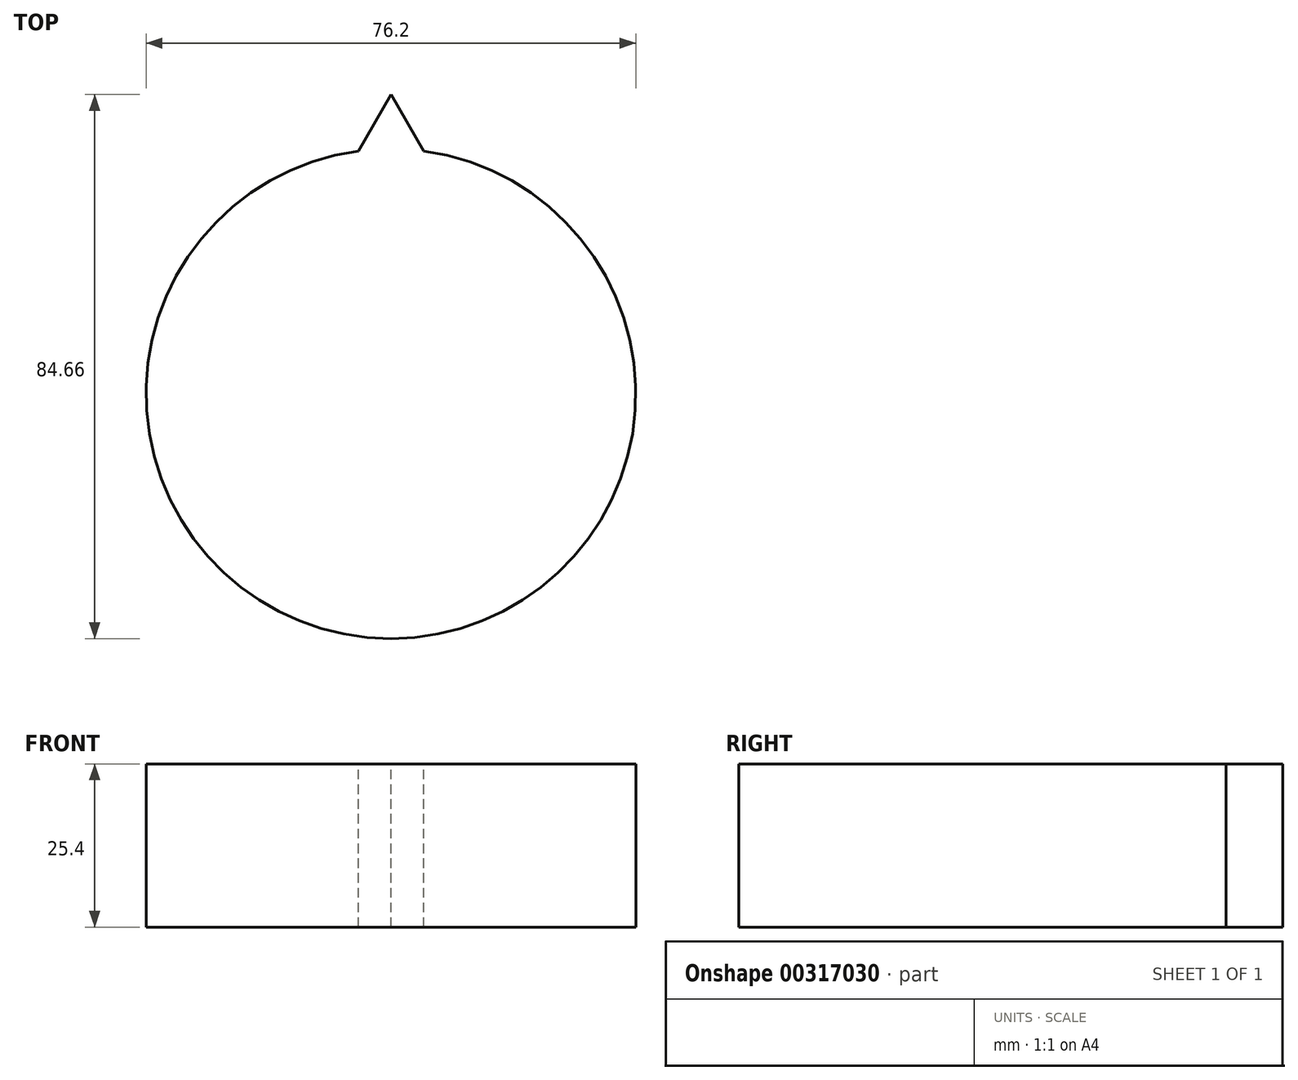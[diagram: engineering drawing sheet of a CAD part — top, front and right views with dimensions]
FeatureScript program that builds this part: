
annotation { "Feature Type Name" : "Feature", "Feature Type Description" : "" }
export const myFeature = defineFeature(function(context is Context, id is Id, definition is map)
    precondition{}
    {
        {
            var Q0;
            Q0=qCreatedBy(makeId("Top.planeOp"),FACE);
            var sketch = newSketch(context, id + "F0", { "sketchPlane" : qUnion([Q0])});
            skCircle(sketch, "E0", {"center": v(0, 0) * mm, "radius": 38.1 * mm});
            skSolve(sketch);
        }
        {
            var Q0;
            Q0 = qSketchRegion(id + "F0", true);
            extrude(context, id + "F1", {"entities" : qUnion([Q0]), "depth" : 25.4 * mm});
        }
        {
            var Q0;
            Q0=makeQuery(id+"F1.opExtrude","CAP_FACE",FACE,{"disambiguationData":[OSD([sQuery(id+"F0.wireOp",EDGE,"E0")])],"isStart":false});
            var sketch = newSketch(context, id + "F2", { "sketchPlane" : qUnion([Q0])});
            skLineSegment(sketch, "E1", {"start": v(0, 0) * mm, "end": v(0, 46.35) * mm, "construction": true});
            skLineSegment(sketch, "E2", {"start": v(-5.08, 37.76) * mm, "end": v(5.08, 37.76) * mm});
            skLineSegment(sketch, "E3", {"start": v(-5.08, 37.76) * mm, "end": v(0, 46.56) * mm});
            skLineSegment(sketch, "E4", {"start": v(5.08, 37.76) * mm, "end": v(0, 46.56) * mm});
            skSolve(sketch);
        }
        {
            var Q0;
            Q0 = qSketchRegion(id + "F2", true);
            extrude(context, id + "F3", {"entities" : qUnion([Q0]), "operationType" : NewBodyOperationType.ADD, "oppositeDirection" : true, "depth" : 25.4 * mm});
        }
    });
